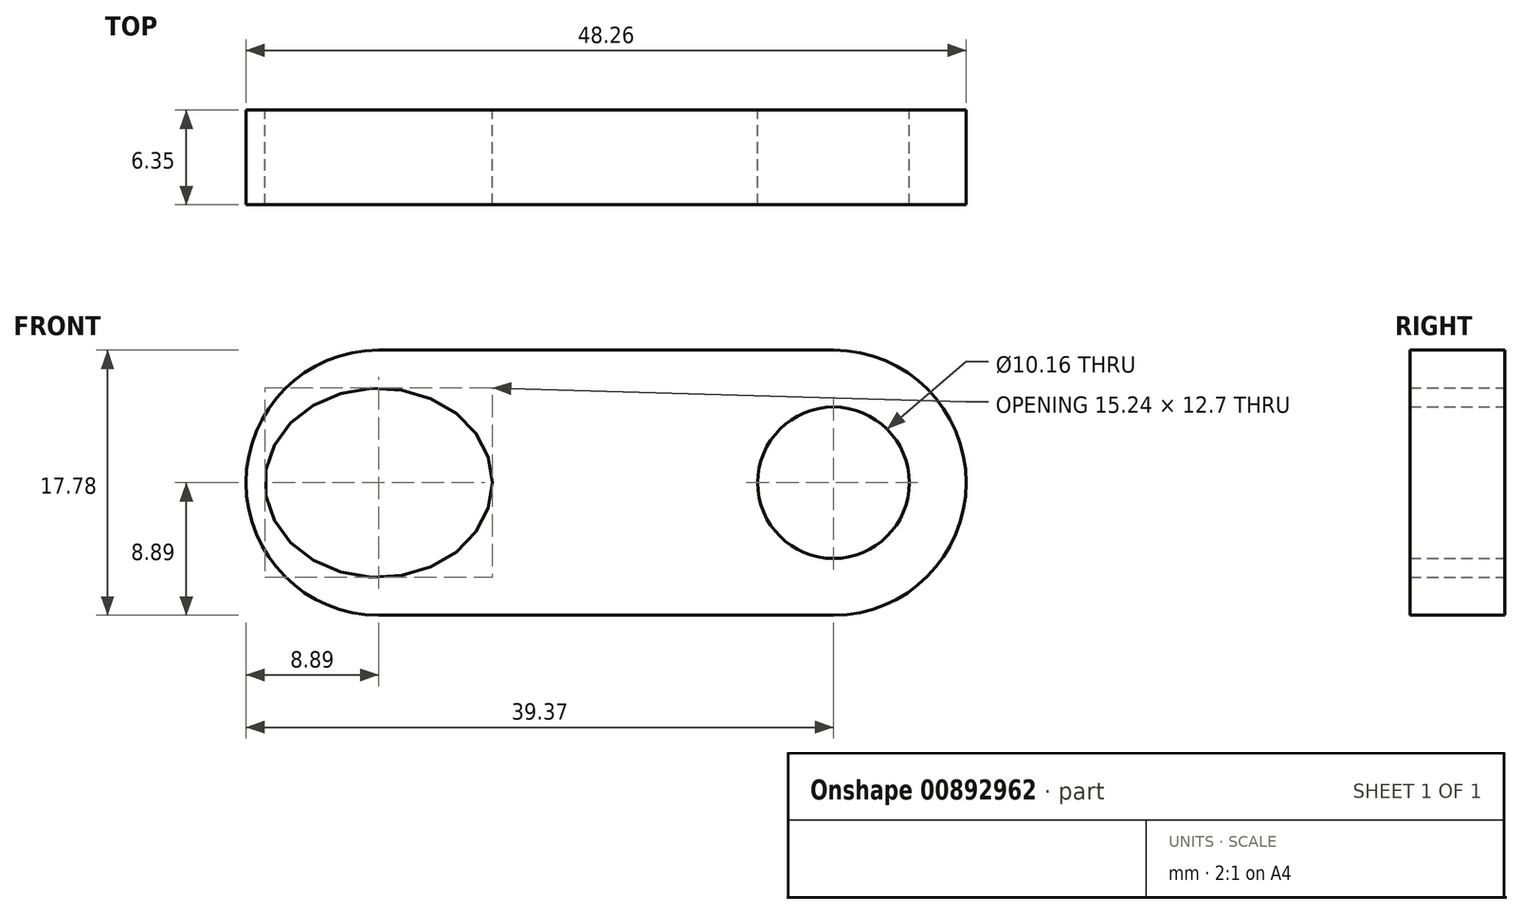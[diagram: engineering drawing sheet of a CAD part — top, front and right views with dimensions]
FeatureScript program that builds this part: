
annotation { "Feature Type Name" : "Feature", "Feature Type Description" : "" }
export const myFeature = defineFeature(function(context is Context, id is Id, definition is map)
    precondition{}
    {
        {
            var Q0;
            Q0=qCreatedBy(makeId("Front.planeOp"),FACE);
            var sketch = newSketch(context, id + "F0", { "sketchPlane" : qUnion([Q0])});
            skLineSegment(sketch, "E0", {"start": v(0, 0) * mm, "end": v(30.48, 0) * mm, "construction": true});
            skArc(sketch, "E1", {"start": v(0, 8.9) * mm, "mid": v(-8.9, 0) * mm, "end": v(0, -8.9) * mm});
            skLineSegment(sketch, "E2", {"start": v(0, 8.9) * mm, "end": v(30.48, 8.9) * mm});
            skLineSegment(sketch, "E3", {"start": v(0, -8.9) * mm, "end": v(30.48, -8.9) * mm});
            skArc(sketch, "E4", {"start": v(30.48, -8.9) * mm, "mid": v(39.37, 0) * mm, "end": v(30.48, 8.9) * mm});
            skEllipse(sketch, "E5", {"center": v(0, 0) * mm, "majorRadius": 7.62 * mm, "minorRadius": 6.35 * mm, "majorAxis": v(1, 0)});
            skCircle(sketch, "E6", {"center": v(30.48, 0) * mm, "radius": 5.08 * mm});
            skSolve(sketch);
        }
        {
            var Q0;
            Q0 = qSketchRegion(id + "F0", true);
            extrude(context, id + "F1", {"entities" : qUnion([Q0]), "depth" : 6.35 * mm, "offsetDistance" : 25.4 * mm});
        }
    });
